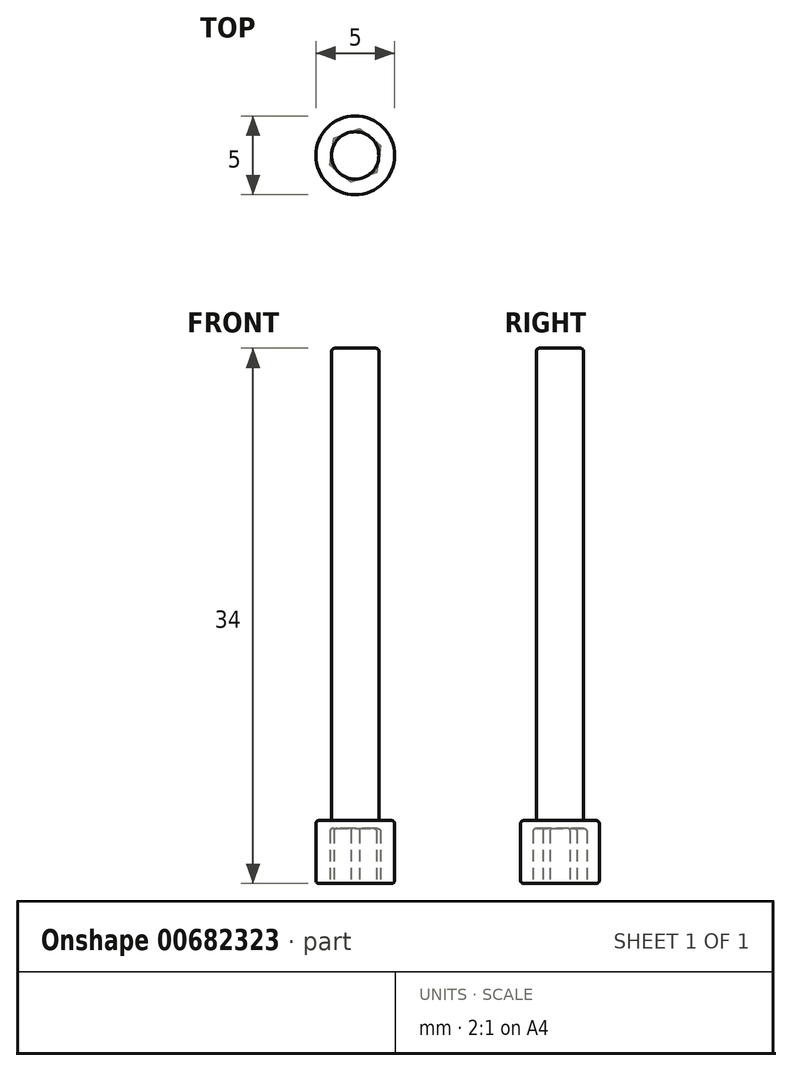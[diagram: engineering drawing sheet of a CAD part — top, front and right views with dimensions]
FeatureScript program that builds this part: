
annotation { "Feature Type Name" : "Feature", "Feature Type Description" : "" }
export const myFeature = defineFeature(function(context is Context, id is Id, definition is map)
    precondition{}
    {
        {
            var Q0;
            Q0=qCreatedBy(makeId("Top.planeOp"),FACE);
            var sketch = newSketch(context, id + "F0", { "sketchPlane" : qUnion([Q0])});
            skCircle(sketch, "E0", {"center": v(0, 0) * mm, "radius": 2.5 * mm});
            skCircle(sketch, "E1.cCircle", {"center": v(0, 0) * mm, "radius": 1.5 * mm, "construction": true});
            skLineSegment(sketch, "E1.0", {"start": v(0.26, 1.71) * mm, "end": v(1.61, 0.63) * mm});
            skLineSegment(sketch, "E1.1", {"start": v(1.61, 0.63) * mm, "end": v(1.35, -1.08) * mm});
            skLineSegment(sketch, "E1.2", {"start": v(1.35, -1.08) * mm, "end": v(-0.26, -1.71) * mm});
            skLineSegment(sketch, "E1.3", {"start": v(-0.26, -1.71) * mm, "end": v(-1.61, -0.63) * mm});
            skLineSegment(sketch, "E1.4", {"start": v(-1.61, -0.63) * mm, "end": v(-1.35, 1.08) * mm});
            skLineSegment(sketch, "E1.5", {"start": v(-1.35, 1.08) * mm, "end": v(0.26, 1.71) * mm});
            skPoint(sketch, "E1.0.midPoint", {"position": v(0.94, 1.17) * mm});
            skSolve(sketch);
        }
        {
            var Q0;
            Q0=makeQuery(id+"F0.imprint","IMPRINT",FACE,{"disambiguationData":[TD([[makeQuery(id+"F0.imprint","IMPRINT",EDGE,{"derivedFrom":sQuery(id+"F0.wireOp",EDGE,"E0")}),1.0]])]});
            var Q1;
            Q1=makeQuery(id+"F0.imprint","IMPRINT",FACE,{"disambiguationData":[TD([[makeQuery(id+"F0.imprint","IMPRINT",EDGE,{"derivedFrom":sQuery(id+"F0.wireOp",EDGE,"E1.0")}),-1.0]])]});
            extrude(context, id + "F1", {"entities" : qUnion([Q0, Q1]), "depth" : 4 * mm, "offsetDistance" : 25 * mm});
        }
        {
            var Q0;
            Q0=makeQuery(id+"F0.imprint","IMPRINT",FACE,{"disambiguationData":[TD([[makeQuery(id+"F0.imprint","IMPRINT",EDGE,{"derivedFrom":sQuery(id+"F0.wireOp",EDGE,"E1.0")}),-1.0]])]});
            extrude(context, id + "F2", {"entities" : qUnion([Q0]), "operationType" : NewBodyOperationType.REMOVE, "depth" : 3.5 * mm, "offsetDistance" : 25 * mm});
        }
        {
            var Q0;
            Q0=makeQuery(id+"F1.opExtrude","CAP_FACE",FACE,{"disambiguationData":[OSD([sQuery(id+"F0.wireOp",EDGE,"E0")])],"isStart":false});
            var sketch = newSketch(context, id + "F3", { "sketchPlane" : qUnion([Q0])});
            skCircle(sketch, "E2", {"center": v(0, 0) * mm, "radius": 1.5 * mm});
            skSolve(sketch);
        }
        {
            var Q0;
            Q0 = qSketchRegion(id + "F3", true);
            extrude(context, id + "F4", {"entities" : qUnion([Q0]), "operationType" : NewBodyOperationType.ADD, "depth" : 30 * mm, "offsetDistance" : 25 * mm});
        }
        {
            var Q0;
            Q0=makeQuery(id+"F4.opExtrude","CAP_EDGE",EDGE,{"disambiguationData":[OSD([sQuery(id+"F3.wireOp",EDGE,"E2")])],"isStart":true});
            var Q1;
            Q1=makeQuery(id+"F4.opExtrude","CAP_FACE",FACE,{"disambiguationData":[OSD([sQuery(id+"F3.wireOp",EDGE,"E2")])],"isStart":false});
            var Q2;
            Q2=makeQuery(id+"F1.opExtrude","SWEPT_FACE",FACE,{"disambiguationData":[OSD([sQuery(id+"F0.wireOp",EDGE,"E0")])]});
            var Q3;
            Q3=makeQuery(id+"F2.boolean.opBoolean","COPY",EDGE,{"derivedFrom":makeQuery(id+"F2.opExtrude","CAP_EDGE",EDGE,{"disambiguationData":[OSD([sQuery(id+"F0.wireOp",EDGE,"E1.5")])],"isStart":true})});
            var Q4;
            Q4=makeQuery(id+"F2.boolean.opBoolean","COPY",FACE,{"derivedFrom":makeQuery(id+"F2.opExtrude","CAP_FACE",FACE,{"disambiguationData":[OSD([sQuery(id+"F0.wireOp",EDGE,"E1.0"),sQuery(id+"F0.wireOp",EDGE,"E1.1"),sQuery(id+"F0.wireOp",EDGE,"E1.2"),sQuery(id+"F0.wireOp",EDGE,"E1.3"),sQuery(id+"F0.wireOp",EDGE,"E1.4"),sQuery(id+"F0.wireOp",EDGE,"E1.5")])],"isStart":false})});
            var Q5;
            Q5=makeQuery(id+"F2.boolean.opBoolean","COPY",EDGE,{"derivedFrom":makeQuery(id+"F2.opExtrude","CAP_EDGE",EDGE,{"disambiguationData":[OSD([sQuery(id+"F0.wireOp",EDGE,"E1.2")])],"isStart":true})});
            var Q6;
            Q6=makeQuery(id+"F2.boolean.opBoolean","COPY",EDGE,{"derivedFrom":makeQuery(id+"F2.opExtrude","CAP_EDGE",EDGE,{"disambiguationData":[OSD([sQuery(id+"F0.wireOp",EDGE,"E1.3")])],"isStart":true})});
            var Q7;
            Q7=makeQuery(id+"F2.boolean.opBoolean","COPY",EDGE,{"derivedFrom":makeQuery(id+"F2.opExtrude","CAP_EDGE",EDGE,{"disambiguationData":[OSD([sQuery(id+"F0.wireOp",EDGE,"E1.4")])],"isStart":true})});
            var Q8;
            Q8=makeQuery(id+"F2.boolean.opBoolean","COPY",EDGE,{"derivedFrom":makeQuery(id+"F2.opExtrude","CAP_EDGE",EDGE,{"disambiguationData":[OSD([sQuery(id+"F0.wireOp",EDGE,"E1.0")])],"isStart":true})});
            var Q9;
            Q9=makeQuery(id+"F2.boolean.opBoolean","COPY",EDGE,{"derivedFrom":makeQuery(id+"F2.opExtrude","CAP_EDGE",EDGE,{"disambiguationData":[OSD([sQuery(id+"F0.wireOp",EDGE,"E1.1")])],"isStart":true})});
            fillet(context, id + "F5", {"entities" : qUnion([Q0, Q1, Q2, Q3, Q4, Q5, Q6, Q7, Q8, Q9]), "radius" : .2 * mm, "tangentPropagation" : true, "allowEdgeOverflow" : false});
        }
    });
